# Revit family: EH 60
name_source: partatom
category: Specialty Equipment
revit_build: Autodesk Revit 2017 (Build: 20160225_1515(x64)
units: mm (PartAtom-declared; Revit-internal decimal feet)

## family parameters
Cut with Voids When Loaded = Yes
Host = Face
Part Type = Normal
Room Calculation Point = No
Round Connector Dimension = Use Diameter
Shared = No

## types (1)
- EH 60 4G AI CI
    Alto encastre = -80 mm
    Ca_1_Cable de conexión = 900 mm
    Ca_1_Frecuencia Hz. = 50/60
    Ca_1_Potencia nominal max. W. = 0.6
    Ca_2_Funcionamiento con gas butano, propano = Yes
    Ca_2_Funcionamiento con gas natural = Yes
    Ca_2_Potencia máxima Kw = 6.9
    Ca_3_Quemador auxiliar - 0.9 Kw = -
    Ca_3_Quemador auxiliar - 1.00 Kw = 1
    Ca_3_Quemador doble anillo - 4.00 Kw = -
    Ca_3_Quemador rápido - 2.8 Kw = 1
    Ca_3_Quemador rápido - 3.00 Kw = -
    Ca_3_Quemador semi-rápido - 1.75 Kw = 2
    Ca_3_Quemador tipo pecera - 2.8 Kw = -
    Ca_3_Quemador triple anillo - 3.1 Kw = -
    Ca_3_Quemador triple anillo - 3.35 Kw = -
    Ca_4_Autoencendido (AI) = Yes
    Ca_4_Cristal biselado = No
    Ca_4_Esquinas Redondeadas = Yes
    Ca_4_Lámpara indicativa de poder = No
    Ca_4_Seguridad por termopar (AL) = No
    Ca_5_Complemento para parrillas = No
    Ca_5_Complemento para recipientes pequeños = No
    Ca_5_Inyectores para gas natural = Yes
    Ca_5_Parrilla esmaltada = No
    Ca_5_Parrilla esmalte mate = No
    Ca_5_Parrilla hierro fundido = Yes
    Ca_5_Parrilla hierro fundido individuales = No
    Ca_5_Parrillas individuales esmaltadas = No
    Ca_Alto = 83 mm
    Ca_Ancho = 580 mm  [stored 1.90289 ft]
    Ca_Ancho Interior = 553 mm
    Ca_Certificación (Chile) = G-013-01-166219
    Ca_Creado por = Catálogo Arquitectura
    Ca_Código Catálogo Arquitectura = 465_TEK_031
    Ca_Código EAN = 8421152125472
    Ca_Código del Producto = 40225082
    Ca_Especificaciones Técnicas = Placa de cocción a gas empotrable para cocina modelo EP 60 4G AI TR CI
    Ca_Fabricante = Teka
    Ca_Instalación = Empotrable
    Ca_Itemizado CDT = E 08 06 02
    Ca_Masterformat = 11 30 13.13
    Ca_Material Principal = Acero inoxidable austenítico
    Ca_Medidas de embalaje = 64 x 59 x 12,5
    Ca_País de Fabricación = Italia
    Ca_Peso = 8,0 kg
    Ca_Producto = Placa de cocción a gas EH 60 4G AI CI
    Ca_Profundidad = 500 mm
    Ca_Profundidad Interior = 473 mm
    Ca_Representante = Teka
    Ca_Teléfono = 99821 1017
    Ca_Usos = Placa de cocción a gas empotrable para mueble de cocina
    Ca_Web del Fabricante = www.teka.com
    Ca_Web del Representante = www.teka.cl
    Cubierta encimera = Teka_Acero inoxidable austenítico
    Default Elevation = 1219.2 mm  [stored 4 ft]
    Description = Placa de cocción a gas empotrable para mueble de cocina
    Disco Inducción = Teka_Interior Negro
    Interior encimera = Teka_Aluminio
    Luz encendido = Teka_Menu Luz Roja
    Manufacturer = Teka
    Material Perilla = Teka_Acero Inoxidable Satinado
    Model = EH 60 4G AI CI
    Perilla Goma Negra = Teka_Goma Negra
    Quemador Inox = Teka_Acero inoxidable austenítico
    Quemador Inox-Satinado = Teka_Acero Inoxidable Satinado
    Quemador Negro = Teka_Quemador Negro
    Rejilla Negra = Teka_Quemador Negro
    URL = www.teka.cl
    Voltage = 230V
    Wattage = 0.6

note: [stored X ft] marks values corroborated as IEEE doubles in the binary element streams (Revit-internal decimal feet)

## geometry (parser evidence)
native form markers: Sweep x5
no freeform markers — native parametric forms only
